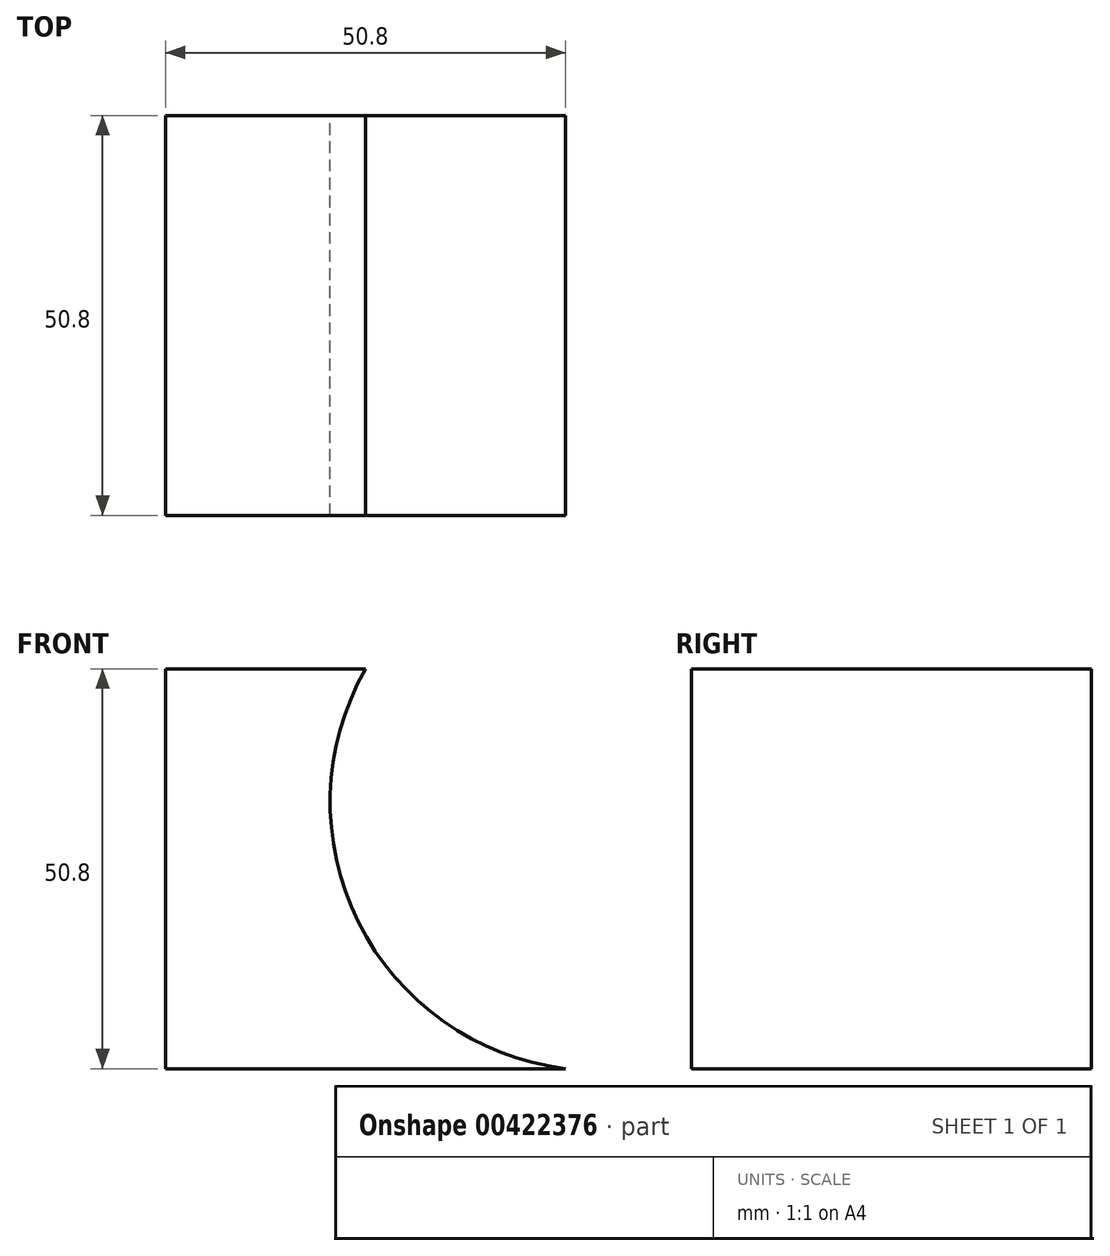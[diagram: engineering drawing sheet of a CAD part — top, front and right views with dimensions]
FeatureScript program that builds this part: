
annotation { "Feature Type Name" : "Feature", "Feature Type Description" : "" }
export const myFeature = defineFeature(function(context is Context, id is Id, definition is map)
    precondition{}
    {
        {
            var Q0;
            Q0=qCreatedBy(makeId("Front.planeOp"),FACE);
            var sketch = newSketch(context, id + "F0", { "sketchPlane" : qUnion([Q0])});
            skLineSegment(sketch, "E0", {"start": v(-47.36, 12.42) * mm, "end": v(-47.36, -38.38) * mm});
            skLineSegment(sketch, "E1", {"start": v(-47.36, -38.38) * mm, "end": v(-47.36, 12.42) * mm});
            skLineSegment(sketch, "E2", {"start": v(-47.36, 12.42) * mm, "end": v(-21.96, 12.42) * mm});
            skLineSegment(sketch, "E3", {"start": v(-47.36, -38.38) * mm, "end": v(3.44, -38.38) * mm});
            skArc(sketch, "E4", {"start": v(-21.96, 12.42) * mm, "mid": v(-22.86, -19.78) * mm, "end": v(3.44, -38.38) * mm});
            skSolve(sketch);
        }
        {
            var Q0;
            Q0 = qSketchRegion(id + "F0", true);
            extrude(context, id + "F1", {"entities" : qUnion([Q0]), "depth" : 50.8 * mm});
        }
    });
